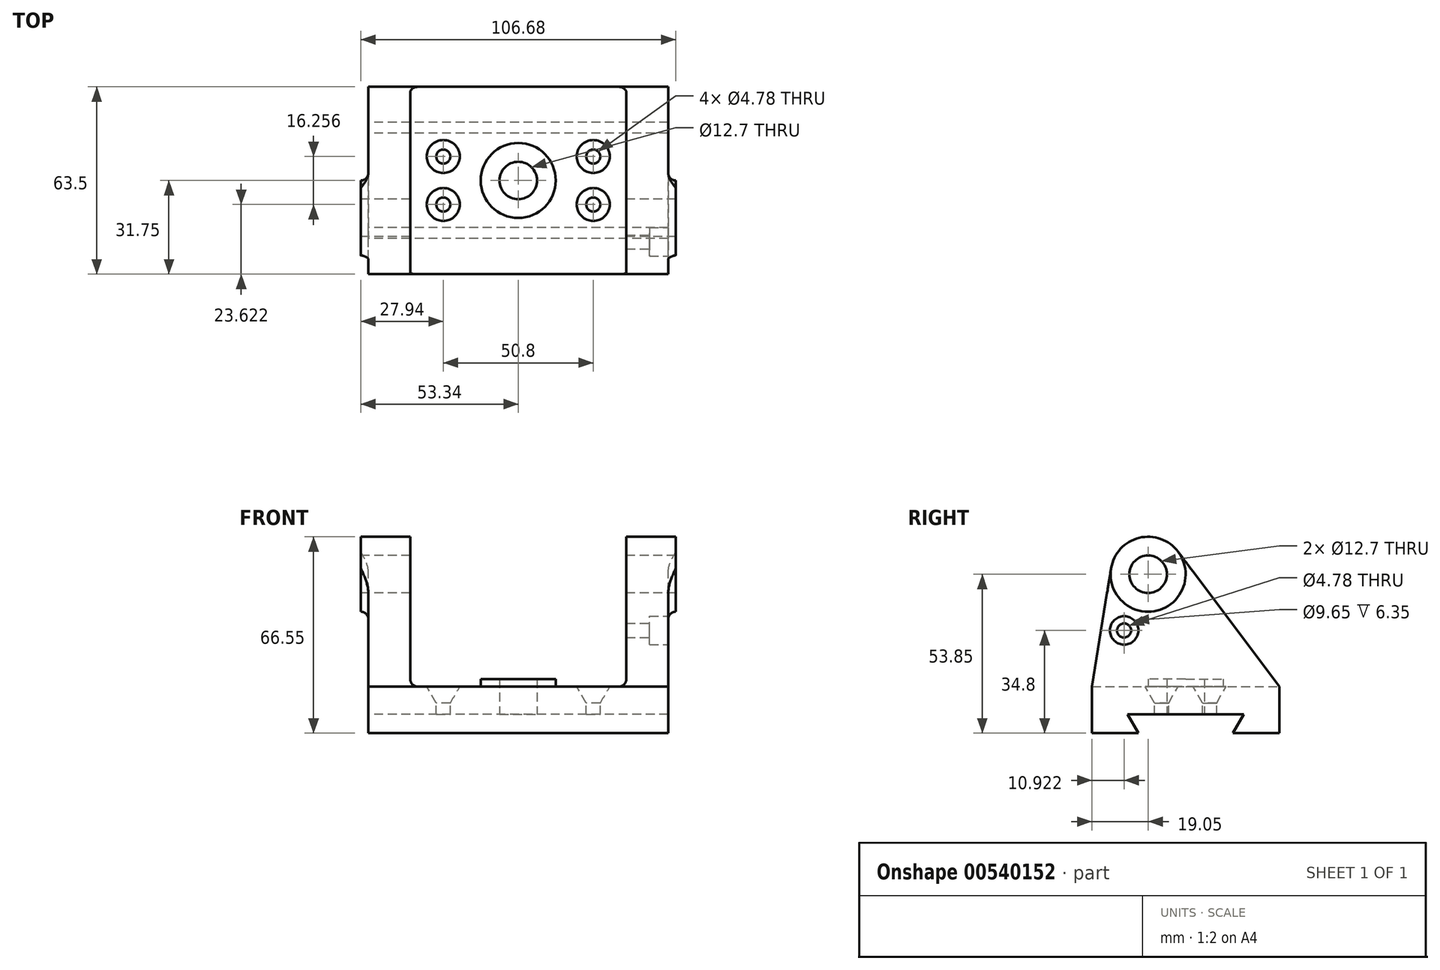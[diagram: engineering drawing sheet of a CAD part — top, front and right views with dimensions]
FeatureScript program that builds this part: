
annotation { "Feature Type Name" : "Feature", "Feature Type Description" : "" }
export const myFeature = defineFeature(function(context is Context, id is Id, definition is map)
    precondition{}
    {
        {
            var Q0;
            Q0=qCreatedBy(makeId("Right.planeOp"),FACE);
            var sketch = newSketch(context, id + "F0", { "sketchPlane" : qUnion([Q0])});
            skLineSegment(sketch, "E0", {"start": v(-86.3, 0) * mm, "end": v(87.75, 0) * mm, "construction": true});
            skLineSegment(sketch, "E1", {"start": v(0, 86.84) * mm, "end": v(0, -84.65) * mm, "construction": true});
            skLineSegment(sketch, "E2", {"start": v(-31.75, 0) * mm, "end": v(-31.75, -15.75) * mm});
            skLineSegment(sketch, "E3", {"start": v(-31.75, -15.75) * mm, "end": v(-16, -15.75) * mm});
            skCircle(sketch, "E4", {"center": v(-12.7, 38.1) * mm, "radius": 6.35 * mm});
            skCircle(sketch, "E5", {"center": v(-12.7, 38.1) * mm, "radius": 12.7 * mm});
            skLineSegment(sketch, "E6", {"start": v(-31.75, 0) * mm, "end": v(-25.24, 40.13) * mm});
            skLineSegment(sketch, "E7", {"start": v(0, -9.4) * mm, "end": v(-19.67, -9.4) * mm});
            skLineSegment(sketch, "E8", {"start": v(-19.67, -9.4) * mm, "end": v(-16, -15.75) * mm});
            skPoint(sketch, "E9.orphan", {"position": v(0, -15.75) * mm});
            skLineSegment(sketch, "E10.MirrorCS", {"start": v(19.67, -9.4) * mm, "end": v(16, -15.75) * mm});
            skLineSegment(sketch, "E11.MirrorCS", {"start": v(31.75, 0) * mm, "end": v(31.75, -15.75) * mm});
            skLineSegment(sketch, "E12.MirrorCS", {"start": v(0, -9.4) * mm, "end": v(19.67, -9.4) * mm});
            skLineSegment(sketch, "E13.MirrorCS", {"start": v(31.75, -15.75) * mm, "end": v(16, -15.75) * mm});
            skLineSegment(sketch, "E14", {"start": v(31.75, 0) * mm, "end": v(-2.54, 45.72) * mm});
            skLineSegment(sketch, "E15", {"start": v(-31.75, 0) * mm, "end": v(31.75, 0) * mm});
            skSolve(sketch);
        }
        {
            var Q0;
            Q0=makeQuery(id+"F0.imprint","IMPRINT",FACE,{"disambiguationData":[TD([[makeQuery(id+"F0.imprint","IMPRINT",EDGE,{"derivedFrom":sQuery(id+"F0.wireOp",EDGE,"E2")}),1.0]])]});
            var Q1;
            Q1=makeQuery(id+"F0.imprint","IMPRINT",FACE,{"disambiguationData":[TD([[makeQuery(id+"F0.imprint","IMPRINT",EDGE,{"derivedFrom":sQuery(id+"F0.wireOp",EDGE,"E4")}),-1.0]])]});
            var Q2;
            {var subQ0=sQuery(id+"F0.wireOp",EDGE,"E6");Q2=makeQuery(id+"F0.imprint","IMPRINT",FACE,{"disambiguationData":[TD([[makeQuery(id+"F0.imprint","IMPRINT",EDGE,{"derivedFrom":subQ0}),-1.0]])]});}
            extrude(context, id + "F1", {"entities" : qUnion([Q0, Q1, Q2]), "endBound" : BoundingType.SYMMETRIC, "depth" : 101.6 * mm, "offsetDistance" : 25.4 * mm});
        }
        {
            var Q0;
            Q0=makeQuery(id+"F0.imprint","IMPRINT",FACE,{"disambiguationData":[TD([[makeQuery(id+"F0.imprint","IMPRINT",EDGE,{"derivedFrom":sQuery(id+"F0.wireOp",EDGE,"E4")}),-1.0]])]});
            extrude(context, id + "F2", {"entities" : qUnion([Q0]), "operationType" : NewBodyOperationType.ADD, "endBound" : BoundingType.SYMMETRIC, "depth" : 106.68 * mm, "offsetDistance" : 25.4 * mm});
        }
        {
            var Q0;
            {var subQ0=sQuery(id+"F0.wireOp",EDGE,"E6");Q0=makeQuery(id+"F0.imprint","IMPRINT",FACE,{"disambiguationData":[TD([[makeQuery(id+"F0.imprint","IMPRINT",EDGE,{"derivedFrom":subQ0}),-1.0]])]});}
            var Q1;
            Q1=makeQuery(id+"F0.imprint","IMPRINT",FACE,{"disambiguationData":[TD([[makeQuery(id+"F0.imprint","IMPRINT",EDGE,{"derivedFrom":sQuery(id+"F0.wireOp",EDGE,"E4")}),-1.0]])]});
            extrude(context, id + "F3", {"entities" : qUnion([Q0, Q1]), "operationType" : NewBodyOperationType.REMOVE, "endBound" : BoundingType.SYMMETRIC, "oppositeDirection" : true, "depth" : 73.15 * mm, "offsetDistance" : 25.4 * mm});
        }
        {
            var Q0;
            Q0=makeQuery(id+"F3.boolean.opBoolean","COPY",FACE,{"derivedFrom":makeQuery(id+"F3.opExtrude","SWEPT_FACE",FACE,{"disambiguationData":[OSD([sQuery(id+"F0.wireOp",EDGE,"E15")])]})});
            var sketch = newSketch(context, id + "F4", { "sketchPlane" : qUnion([Q0])});
            skPoint(sketch, "E16", {"position": v(-25.4, 8.13) * mm});
            skPoint(sketch, "E17", {"position": v(25.4, 8.13) * mm});
            skPoint(sketch, "E18", {"position": v(25.4, -8.13) * mm});
            skPoint(sketch, "E19", {"position": v(-25.4, -8.13) * mm});
            skCircle(sketch, "E20", {"center": v(0, 0) * mm, "radius": 12.7 * mm});
            skCircle(sketch, "E21", {"center": v(0, 0) * mm, "radius": 6.35 * mm});
            skSolve(sketch);
        }
        {
            var Q0;
            Q0=sQuery(id+"F4.wireOp",VERTEX,"E16");
            var Q1;
            Q1=sQuery(id+"F4.wireOp",VERTEX,"E17");
            var Q2;
            Q2=sQuery(id+"F4.wireOp",VERTEX,"E18");
            var Q3;
            Q3=sQuery(id+"F4.wireOp",VERTEX,"E19");
            var Q4;
            Q4=makeQuery(id+"F1.opExtrude","SWEPT_BODY",BODY,{"disambiguationData":[OSD([sQuery(id+"F0.wireOp",EDGE,"E2"),sQuery(id+"F0.wireOp",EDGE,"E3"),sQuery(id+"F0.wireOp",EDGE,"E4"),sQuery(id+"F0.wireOp",EDGE,"E5"),sQuery(id+"F0.wireOp",EDGE,"E6"),sQuery(id+"F0.wireOp",EDGE,"E7"),sQuery(id+"F0.wireOp",EDGE,"E8"),sQuery(id+"F0.wireOp",EDGE,"E10.MirrorCS"),sQuery(id+"F0.wireOp",EDGE,"E11.MirrorCS"),sQuery(id+"F0.wireOp",EDGE,"E12.MirrorCS"),sQuery(id+"F0.wireOp",EDGE,"E13.MirrorCS"),sQuery(id+"F0.wireOp",EDGE,"E14")])]});
            hole(context, id + "F5", {"style" : HoleStyle.C_SINK, "endStyle" : HoleEndStyle.THROUGH, "holeDiameter" : 4.78 * mm, "cSinkDiameter" : 11.18 * mm, "cSinkAngle" : 60 * degree, "isTappedThrough" : true, "tappedDepth" : 12.7 * mm, "tapClearance" : 3, "startFromSketch" : true, "locations" : qUnion([Q0, Q1, Q2, Q3]), "scope" : qUnion([Q4])});
        }
        {
            var Q0;
            Q0 = qSketchRegion(id + "F4", true);
            extrude(context, id + "F6", {"entities" : qUnion([Q0]), "operationType" : NewBodyOperationType.ADD, "depth" : 2.54 * mm, "offsetDistance" : 25.4 * mm});
        }
        {
            var Q0;
            Q0=makeQuery(id+"F6.boolean.opBoolean","SPLIT",FACE,{"disambiguationData":[TD([makeQuery(id+"F6.opExtrude","SWEPT_FACE",FACE,{"disambiguationData":[OSD([sQuery(id+"F4.wireOp",EDGE,"E21")])]})])],"derivedFrom":makeQuery(id+"F3.boolean.opBoolean","COPY",FACE,{"derivedFrom":makeQuery(id+"F3.opExtrude","SWEPT_FACE",FACE,{"disambiguationData":[OSD([sQuery(id+"F0.wireOp",EDGE,"E15")])]})})});
            extrude(context, id + "F7", {"entities" : qUnion([Q0]), "operationType" : NewBodyOperationType.REMOVE, "endBound" : BoundingType.UP_TO_NEXT, "oppositeDirection" : true, "depth" : 25.4 * mm, "offsetDistance" : 25.4 * mm});
        }
        {
            var Q0;
            Q0=makeQuery(id+"F1.opExtrude","CAP_FACE",FACE,{"disambiguationData":[OSD([sQuery(id+"F0.wireOp",EDGE,"E2"),sQuery(id+"F0.wireOp",EDGE,"E3"),sQuery(id+"F0.wireOp",EDGE,"E4"),sQuery(id+"F0.wireOp",EDGE,"E5"),sQuery(id+"F0.wireOp",EDGE,"E6"),sQuery(id+"F0.wireOp",EDGE,"E7"),sQuery(id+"F0.wireOp",EDGE,"E8"),sQuery(id+"F0.wireOp",EDGE,"E10.MirrorCS"),sQuery(id+"F0.wireOp",EDGE,"E11.MirrorCS"),sQuery(id+"F0.wireOp",EDGE,"E12.MirrorCS"),sQuery(id+"F0.wireOp",EDGE,"E13.MirrorCS"),sQuery(id+"F0.wireOp",EDGE,"E14")])],"isStart":false});
            var sketch = newSketch(context, id + "F8", { "sketchPlane" : qUnion([Q0])});
            skPoint(sketch, "E22", {"position": v(-20.83, 19.05) * mm});
            skSolve(sketch);
        }
        {
            var Q0;
            Q0=sQuery(id+"F8.wireOp",VERTEX,"E22");
            var Q1;
            Q1=makeQuery(id+"F1.opExtrude","SWEPT_BODY",BODY,{"disambiguationData":[OSD([sQuery(id+"F0.wireOp",EDGE,"E2"),sQuery(id+"F0.wireOp",EDGE,"E3"),sQuery(id+"F0.wireOp",EDGE,"E4"),sQuery(id+"F0.wireOp",EDGE,"E5"),sQuery(id+"F0.wireOp",EDGE,"E6"),sQuery(id+"F0.wireOp",EDGE,"E7"),sQuery(id+"F0.wireOp",EDGE,"E8"),sQuery(id+"F0.wireOp",EDGE,"E10.MirrorCS"),sQuery(id+"F0.wireOp",EDGE,"E11.MirrorCS"),sQuery(id+"F0.wireOp",EDGE,"E12.MirrorCS"),sQuery(id+"F0.wireOp",EDGE,"E13.MirrorCS"),sQuery(id+"F0.wireOp",EDGE,"E14")])]});
            hole(context, id + "F9", {"style" : HoleStyle.C_BORE, "endStyle" : HoleEndStyle.BLIND, "holeDiameter" : 4.78 * mm, "cBoreDiameter" : 9.65 * mm, "cBoreDepth" : 6.35 * mm, "holeDepth" : 16.76 * mm, "isTappedThrough" : true, "tappedDepth" : 12.7 * mm, "tapClearance" : 3, "startFromSketch" : true, "locations" : qUnion([Q0]), "scope" : qUnion([Q1])});
        }
        {
            var Q0;
            Q0=makeQuery(id+"F6.opExtrude","CAP_EDGE",EDGE,{"disambiguationData":[OSD([sQuery(id+"F4.wireOp",EDGE,"E20")])],"isStart":true});
            var Q1;
            Q1=makeQuery(id+"F3.boolean.opBoolean","COPY",EDGE,{"derivedFrom":makeQuery(id+"F3.opExtrude","CAP_EDGE",EDGE,{"disambiguationData":[OSD([sQuery(id+"F0.wireOp",EDGE,"E15")])],"isStart":false})});
            var Q2;
            Q2=makeQuery(id+"F3.boolean.opBoolean","COPY",EDGE,{"derivedFrom":makeQuery(id+"F3.opExtrude","CAP_EDGE",EDGE,{"disambiguationData":[OSD([sQuery(id+"F0.wireOp",EDGE,"E15")])],"isStart":true})});
            var Q3;
            {var subQ0=sQuery(id+"F0.wireOp",EDGE,"E5");Q3=makeQuery(id+"F2.boolean.opBoolean","INTERSECT",EDGE,{"derivedFrom":[makeQuery(id+"F1.opExtrude","CAP_FACE",FACE,{"disambiguationData":[OSD([sQuery(id+"F0.wireOp",EDGE,"E2"),sQuery(id+"F0.wireOp",EDGE,"E3"),sQuery(id+"F0.wireOp",EDGE,"E4"),subQ0,sQuery(id+"F0.wireOp",EDGE,"E6"),sQuery(id+"F0.wireOp",EDGE,"E7"),sQuery(id+"F0.wireOp",EDGE,"E8"),sQuery(id+"F0.wireOp",EDGE,"E10.MirrorCS"),sQuery(id+"F0.wireOp",EDGE,"E11.MirrorCS"),sQuery(id+"F0.wireOp",EDGE,"E12.MirrorCS"),sQuery(id+"F0.wireOp",EDGE,"E13.MirrorCS"),sQuery(id+"F0.wireOp",EDGE,"E14")])],"isStart":false}),makeQuery(id+"F2.opExtrude","SWEPT_FACE",FACE,{"disambiguationData":[OSD([subQ0])]})]});}
            var Q4;
            {var subQ0=sQuery(id+"F0.wireOp",EDGE,"E5");Q4=makeQuery(id+"F2.boolean.opBoolean","INTERSECT",EDGE,{"derivedFrom":[makeQuery(id+"F1.opExtrude","CAP_FACE",FACE,{"disambiguationData":[OSD([sQuery(id+"F0.wireOp",EDGE,"E2"),sQuery(id+"F0.wireOp",EDGE,"E3"),sQuery(id+"F0.wireOp",EDGE,"E4"),subQ0,sQuery(id+"F0.wireOp",EDGE,"E6"),sQuery(id+"F0.wireOp",EDGE,"E7"),sQuery(id+"F0.wireOp",EDGE,"E8"),sQuery(id+"F0.wireOp",EDGE,"E10.MirrorCS"),sQuery(id+"F0.wireOp",EDGE,"E11.MirrorCS"),sQuery(id+"F0.wireOp",EDGE,"E12.MirrorCS"),sQuery(id+"F0.wireOp",EDGE,"E13.MirrorCS"),sQuery(id+"F0.wireOp",EDGE,"E14")])],"isStart":true}),makeQuery(id+"F2.opExtrude","SWEPT_FACE",FACE,{"disambiguationData":[OSD([subQ0])]})]});}
            fillet(context, id + "F10", {"entities" : qUnion([Q0, Q1, Q2, Q3, Q4]), "radius" : 2.54 * mm, "tangentPropagation" : true, "allowEdgeOverflow" : false});
        }
    });
